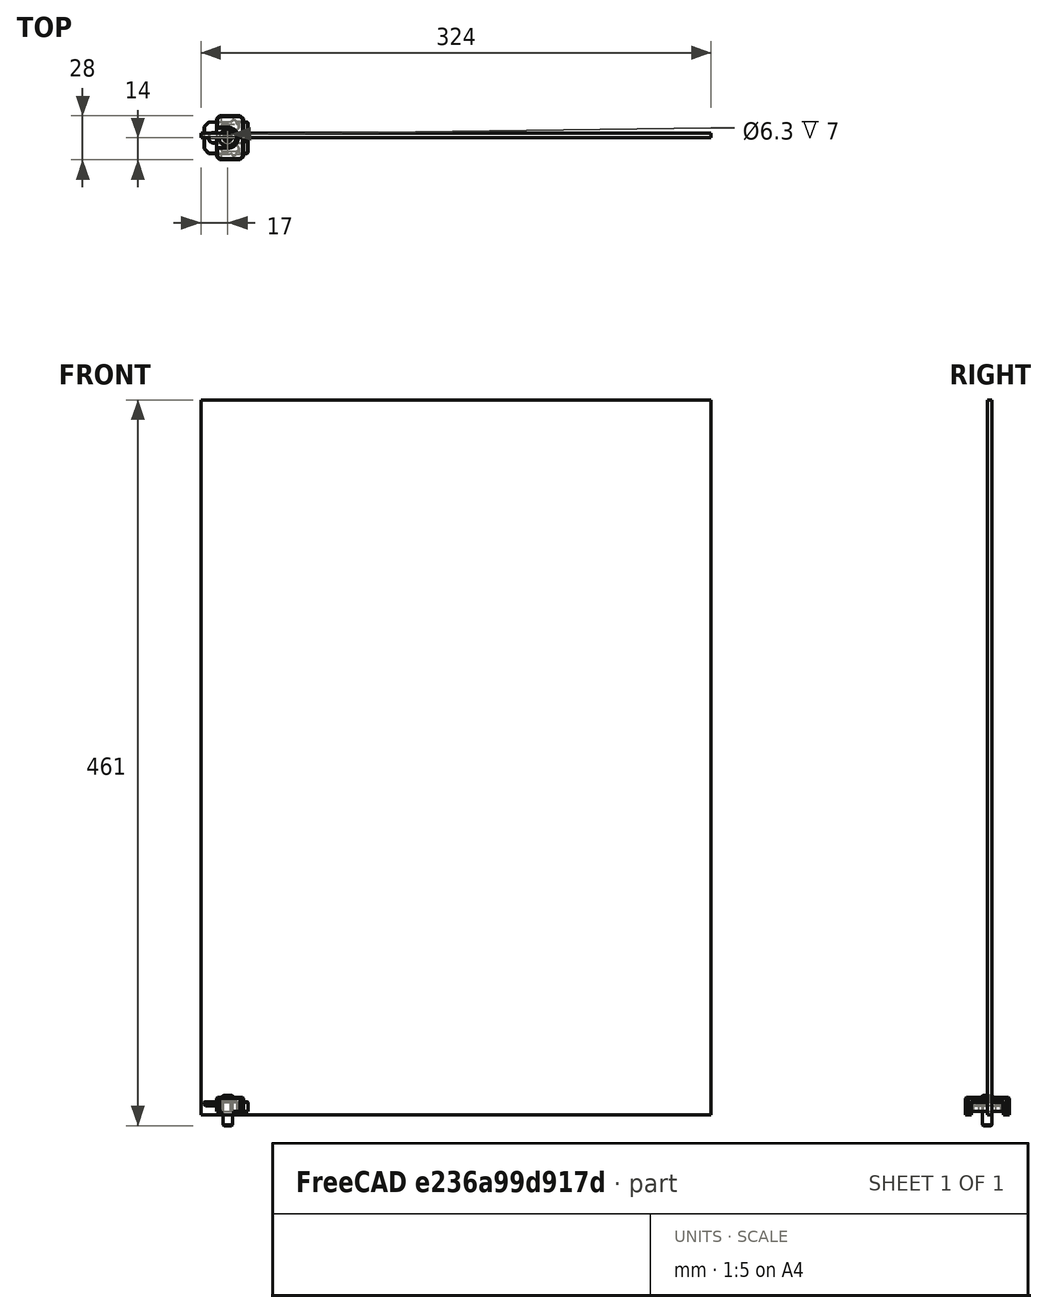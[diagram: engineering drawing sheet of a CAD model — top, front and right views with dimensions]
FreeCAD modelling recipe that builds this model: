
FCSTD DOCUMENT  (FreeCAD 0.19R24291 (Git))
Label: right-panel-assembly
License: All rights reserved
LicenseURL: http://en.wikipedia.org/wiki/All_rights_reserved
objects: Part::Feature×24, App::Part×13, Part::FeaturePython×12, PartDesign::CoordinateSystem×1, Part::Box×1
note: 38 computed .brp shape members not serialized (recipe doc carries the construction recipe); baked Part::Feature solids carry a one-line shape summary decoded from their .brp

FEATURE [Part::Feature] Chamfer008001013  label="mounter-inner"
  shape: bbox 28 x 22 x 6 mm, 82 faces (baked)
FEATURE [Part::FeaturePython] Screw055  label="M6x16-Screw001"  # Fasteners workbench fastener (typed FeaturePython)
  Placement = pos=(15,0,7) rot=(0,0,1;0rad)
  baseObject = -> Chamfer008002001003 [Edge135]
  diameter = 4
  invert = false
  length = 3
  lengthCustom = 16
  matchOuter = false
  offset = 0
  thread = false
  type = 40
FEATURE [Part::Feature] Chamfer008002001009  label="mounter-inner004"
  shape: bbox 28 x 22 x 6 mm, 82 faces (baked)
FEATURE [Part::Feature] Chamfer008002001002  label="mounter-inner001"
  shape: bbox 28 x 22 x 6 mm, 82 faces (baked)
FEATURE [Part::Feature] Chamfer008002001004  label="mounter-inner002"
  shape: bbox 28 x 22 x 6 mm, 82 faces (baked)
FEATURE [Part::Feature] Chamfer008002001007  label="mounter-outer008"
  shape: bbox 17 x 28 x 11 mm, 53 faces (baked)
FEATURE [Part::Feature] Chamfer008002001016  label="mounter-inner008"
  shape: bbox 28 x 22 x 6 mm, 82 faces (baked)
FEATURE [Part::FeaturePython] Screw063  label="M6x16-Screw013"  # Fasteners workbench fastener (typed FeaturePython)
  Placement = pos=(15,0,7) rot=(0,0,1;0rad)
  baseObject = -> Chamfer008002001019 [Edge135]
  diameter = 4
  invert = false
  length = 3
  lengthCustom = 16
  matchOuter = false
  offset = 0
  thread = false
  type = 40
FEATURE [Part::Feature] Chamfer008002001022  label="mounter-inner011"
  shape: bbox 28 x 22 x 6 mm, 82 faces (baked)
FEATURE [Part::Feature] Chamfer008002001011  label="mounter-inner005"
  shape: bbox 28 x 22 x 6 mm, 82 faces (baked)
FEATURE [Part::FeaturePython] Screw057  label="M6x16-Screw003"  # Fasteners workbench fastener (typed FeaturePython)
  Placement = pos=(15,0,7) rot=(0,0,1;0rad)
  baseObject = -> Chamfer008002001007 [Edge135]
  diameter = 4
  invert = false
  length = 3
  lengthCustom = 16
  matchOuter = false
  offset = 0
  thread = false
  type = 40
FEATURE [Part::FeaturePython] Screw054  label="M6x16-Screw007"  # Fasteners workbench fastener (typed FeaturePython)
  Placement = pos=(15,0,7) rot=(0,0,1;0rad)
  baseObject = -> Chamfer008002001001 [Edge135]
  diameter = 4
  invert = false
  length = 3
  lengthCustom = 16
  matchOuter = false
  offset = 0
  thread = false
  type = 40
FEATURE [Part::Feature] Chamfer008002001012  label="mounter-outer005"
  shape: bbox 17 x 28 x 11 mm, 53 faces (baked)
FEATURE [Part::FeaturePython] Screw056  label="M6x16-Screw002"  # Fasteners workbench fastener (typed FeaturePython)
  Placement = pos=(15,0,7) rot=(0,0,1;0rad)
  baseObject = -> Chamfer008002001005 [Edge135]
  diameter = 4
  invert = false
  length = 3
  lengthCustom = 16
  matchOuter = false
  offset = 0
  thread = false
  type = 40
FEATURE [Part::Feature] Chamfer008002001020  label="mounter-outer001"
  shape: bbox 17 x 28 x 11 mm, 53 faces (baked)
FEATURE [Part::Feature] Chamfer008002001003  label="mounter-outer010"
  shape: bbox 17 x 28 x 11 mm, 53 faces (baked)
FEATURE [Part::FeaturePython] Screw062  label="M6x16-Screw012"  # Fasteners workbench fastener (typed FeaturePython)
  Placement = pos=(15,0,7) rot=(0,0,1;0rad)
  baseObject = -> Chamfer008002001017 [Edge135]
  diameter = 4
  invert = false
  length = 3
  lengthCustom = 16
  matchOuter = false
  offset = 0
  thread = false
  type = 40
FEATURE [Part::FeaturePython] Screw060  label="M6x16-Screw010"  # Fasteners workbench fastener (typed FeaturePython)
  Placement = pos=(15,0,7) rot=(0,0,1;0rad)
  baseObject = -> Chamfer008002001012 [Edge135]
  diameter = 4
  invert = false
  length = 3
  lengthCustom = 16
  matchOuter = false
  offset = 0
  thread = false
  type = 40
FEATURE [Part::Feature] Chamfer008002001013  label="mounter-inner006"
  shape: bbox 28 x 22 x 6 mm, 82 faces (baked)
FEATURE [Part::Feature] Chamfer008002001019  label="mounter-outer002"
  shape: bbox 17 x 28 x 11 mm, 53 faces (baked)
FEATURE [Part::Feature] Chamfer008002001006  label="mounter-inner003"
  shape: bbox 28 x 22 x 6 mm, 82 faces (baked)
FEATURE [App::Part] Part016  label="Panel-mounterr2-003"
  Group = -> [Chamfer008002001006,Chamfer008002001007,Screw057]
  Origin = -> Origin016
  Placement = pos=(315,3,39) rot=(-1,0,0;4.71239rad)
FEATURE [Part::FeaturePython] Screw064  label="M6x16-Screw014"  # Fasteners workbench fastener (typed FeaturePython)
  Placement = pos=(15,0,7) rot=(0,0,1;0rad)
  baseObject = -> Chamfer008002001020 [Edge135]
  diameter = 4
  invert = false
  length = 3
  lengthCustom = 16
  matchOuter = false
  offset = 0
  thread = false
  type = 40
FEATURE [PartDesign::CoordinateSystem] LCS_right_panel  label="LCS_right-panel"
  AttacherType = Attacher::AttachEngine3D
FEATURE [Part::Feature] Chamfer008002001023  label="mounter-outer"
  shape: bbox 17 x 28 x 11 mm, 53 faces (baked)
FEATURE [Part::Feature] Chamfer008002001018  label="mounter-inner009"
  shape: bbox 28 x 22 x 6 mm, 82 faces (baked)
FEATURE [App::Part] Part022  label="Panel-mounterr2-009"
  Group = -> [Chamfer008002001018,Chamfer008002001019,Screw063]
  Origin = -> Origin022
  Placement = pos=(39,3,445) rot=(-0.57735,0.57735,-0.57735;4.18879rad)
FEATURE [Part::Feature] Chamfer008002001001  label="mounter-outer011"
  shape: bbox 17 x 28 x 11 mm, 53 faces (baked)
FEATURE [App::Part] Part013  label="Panel-mounterr2-000"
  Group = -> [Chamfer008001013,Chamfer008002001001,Screw054]
  Origin = -> Origin013
  Placement = pos=(39,3,5) rot=(-0.57735,-0.57735,0.57735;4.18879rad)
FEATURE [Part::Feature] Chamfer008002001014  label="mounter-inner007"
  shape: bbox 28 x 22 x 6 mm, 82 faces (baked)
FEATURE [Part::Feature] Chamfer008002001008  label="mounter-outer007"
  shape: bbox 17 x 28 x 11 mm, 53 faces (baked)
FEATURE [Part::Feature] Chamfer008002001017  label="mounter-outer003"
  shape: bbox 17 x 28 x 11 mm, 53 faces (baked)
FEATURE [App::Part] Part021  label="Panel-mounterr2-008"
  Group = -> [Chamfer008002001016,Chamfer008002001017,Screw062]
  Origin = -> Origin021
  Placement = pos=(5,3,411) rot=(0,0.707107,-0.707107;3.14159rad)
FEATURE [Part::Box] Box002  label="panel-324x454x3mm"
  AttacherType = Attacher::AttachEngine3D
  Height = 454
  Length = 324
  Placement = pos=(-2,0,-2) rot=(0,0,1;0rad)
  Width = 3
FEATURE [Part::Feature] Chamfer008002001015  label="mounter-outer004"
  shape: bbox 17 x 28 x 11 mm, 53 faces (baked)
FEATURE [Part::Feature] Chamfer008002001010  label="mounter-outer006"
  shape: bbox 17 x 28 x 11 mm, 53 faces (baked)
FEATURE [App::Part] Part019  label="Panel-mounterr2-006"
  Group = -> [Chamfer008002001013,Chamfer008002001012,Screw060]
  Origin = -> Origin019
  Placement = pos=(281,3,445) rot=(-0.57735,0.57735,-0.57735;4.18879rad)
FEATURE [Part::FeaturePython] Screw065  label="M6x16-Screw015"  # Fasteners workbench fastener (typed FeaturePython)
  Placement = pos=(15,0,7) rot=(0,0,1;0rad)
  baseObject = -> Chamfer008002001023 [Edge135]
  diameter = 4
  invert = false
  length = 3
  lengthCustom = 16
  matchOuter = false
  offset = 0
  thread = false
  type = 40
FEATURE [Part::FeaturePython] Screw061  label="M6x16-Screw011"  # Fasteners workbench fastener (typed FeaturePython)
  Placement = pos=(15,0,7) rot=(0,0,1;0rad)
  baseObject = -> Chamfer008002001015 [Edge135]
  diameter = 4
  invert = false
  length = 3
  lengthCustom = 16
  matchOuter = false
  offset = 0
  thread = false
  type = 40
FEATURE [App::Part] Part020  label="Panel-mounterr2-007"
  Group = -> [Chamfer008002001014,Chamfer008002001015,Screw061]
  Origin = -> Origin020
  Placement = pos=(160,3,445) rot=(-0.57735,0.57735,-0.57735;4.18879rad)
FEATURE [Part::FeaturePython] Screw058  label="M6x16-Screw008"  # Fasteners workbench fastener (typed FeaturePython)
  Placement = pos=(15,0,7) rot=(0,0,1;0rad)
  baseObject = -> Chamfer008002001008 [Edge135]
  diameter = 4
  invert = false
  length = 3
  lengthCustom = 16
  matchOuter = false
  offset = 0
  thread = false
  type = 40
FEATURE [App::Part] Part017  label="Panel-mounterr2-004"
  Group = -> [Chamfer008002001009,Chamfer008002001008,Screw058]
  Origin = -> Origin017
  Placement = pos=(315,3,215) rot=(-1,0,0;4.71239rad)
FEATURE [App::Part] Part024  label="Panel-mounterr2-011"
  Group = -> [Chamfer008002001022,Chamfer008002001023,Screw065]
  Origin = -> Origin024
  Placement = pos=(5,3,39) rot=(0,0.707107,-0.707107;3.14159rad)
FEATURE [Part::Feature] Chamfer008002001005  label="mounter-outer009"
  shape: bbox 17 x 28 x 11 mm, 53 faces (baked)
FEATURE [App::Part] Part015  label="Panel-mounterr2-002"
  Group = -> [Chamfer008002001004,Chamfer008002001005,Screw056]
  Origin = -> Origin015
  Placement = pos=(280.5,3,5) rot=(-0.57735,-0.57735,0.57735;4.18879rad)
FEATURE [Part::Feature] Chamfer008002001021  label="mounter-inner010"
  shape: bbox 28 x 22 x 6 mm, 82 faces (baked)
FEATURE [App::Part] Part023  label="Panel-mounterr2-010"
  Group = -> [Chamfer008002001021,Chamfer008002001020,Screw064]
  Origin = -> Origin023
  Placement = pos=(5,3,215) rot=(0,0.707107,-0.707107;3.14159rad)
FEATURE [Part::FeaturePython] Screw059  label="M6x16-Screw009"  # Fasteners workbench fastener (typed FeaturePython)
  Placement = pos=(15,0,7) rot=(0,0,1;0rad)
  baseObject = -> Chamfer008002001010 [Edge135]
  diameter = 4
  invert = false
  length = 3
  lengthCustom = 16
  matchOuter = false
  offset = 0
  thread = false
  type = 40
FEATURE [App::Part] Part018  label="Panel-mounterr2-005"
  Group = -> [Chamfer008002001011,Chamfer008002001010,Screw059]
  Origin = -> Origin018
  Placement = pos=(315,3,411) rot=(-1,0,0;4.71239rad)
FEATURE [App::Part] Part014  label="Panel-mounterr2-001"
  Group = -> [Chamfer008002001002,Chamfer008002001003,Screw055]
  Origin = -> Origin014
  Placement = pos=(160,3,5) rot=(-0.57735,-0.57735,0.57735;4.18879rad)
FEATURE [App::Part] Part005  label="right-panel"
  Group = -> [Box002,Part013,Part014,Part015,Part016,Part017,Part018,Part019,Part020,Part021,Part022,Part023,Part024,LCS_right_panel]
  Origin = -> Origin005
